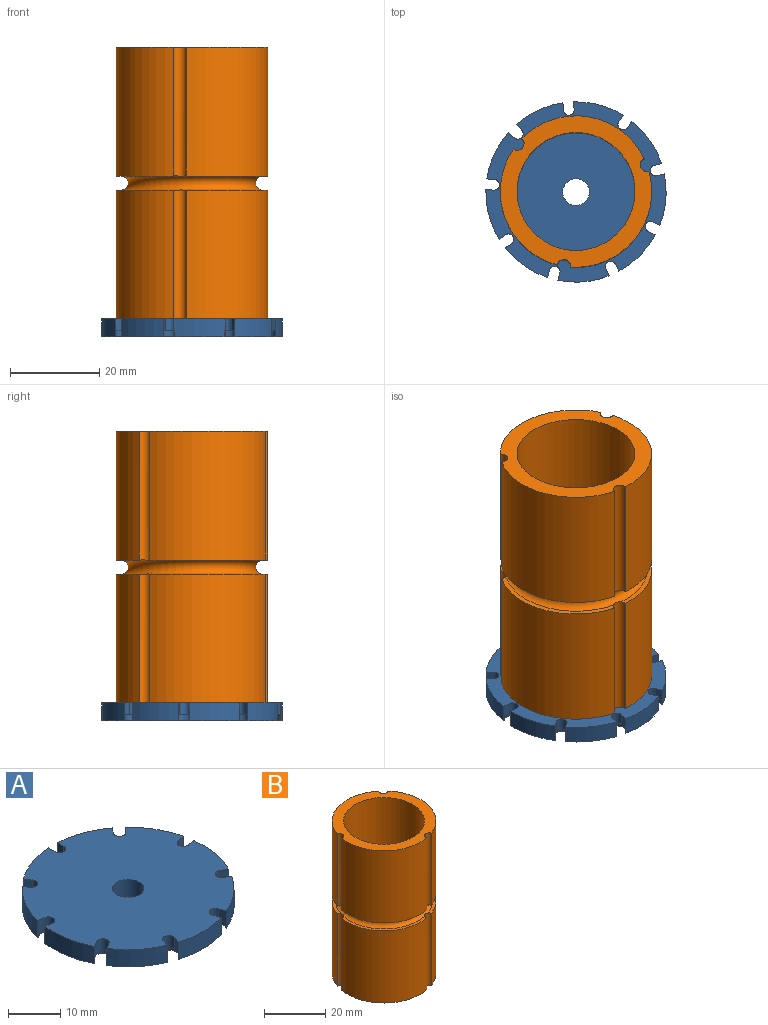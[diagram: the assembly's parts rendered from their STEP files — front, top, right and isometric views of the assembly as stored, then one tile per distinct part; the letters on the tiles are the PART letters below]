
ASSEMBLY  parts=2 mates=2
PART A: 57 faces, bbox 40.5x40.5x4 mm
  f0: plane 4x1.61mm, normal (-0.94,-0.34,0), area 4.8mm2, adj f18,f19,f37,f38,f39,f40
  f1: plane 4x1.48mm, normal (0.5,0.87,0), area 4.8mm2, adj f18,f19,f20,f38,f55,f56
  f2: plane 4x1.48mm, normal (-0.5,-0.87,0), area 4.8mm2, adj f18,f20,f21,f38,f55,f56
  f3: plane 4x1.69mm, normal (-0.17,0.98,0), area 4.8mm2, adj f18,f21,f22,f38,f53,f54
  f4: plane 4x1.69mm, normal (0.17,-0.98,0), area 4.8mm2, adj f18,f22,f23,f38,f53,f54
  f5: plane 4x1.31mm, normal (-0.77,0.64,0), area 4.8mm2, adj f18,f23,f24,f38,f51,f52
  f6: plane 4x1.31mm, normal (0.77,-0.64,0), area 4.8mm2, adj f18,f24,f25,f38,f51,f52
  f7: plane 4x1.71mm, normal (-1,0,0), area 4.8mm2, adj f18,f25,f26,f38,f49,f50
  f8: plane 4x1.71mm, normal (1,0,0), area 4.8mm2, adj f18,f26,f27,f38,f49,f50
  f9: plane 4x1.31mm, normal (-0.77,-0.64,0), area 4.8mm2, adj f18,f27,f28,f38,f47,f48
  f10: plane 4x1.31mm, normal (0.77,0.64,0), area 4.8mm2, adj f18,f28,f29,f38,f47,f48
  f11: plane 4x1.69mm, normal (-0.17,-0.98,0), area 4.8mm2, adj f18,f29,f30,f38,f45,f46
  f12: plane 4x1.69mm, normal (0.17,0.98,0), area 4.8mm2, adj f18,f30,f31,f38,f45,f46
  f13: plane 4x1.48mm, normal (0.5,-0.87,0), area 4.8mm2, adj f18,f31,f32,f38,f43,f44
  f14: plane 4x1.48mm, normal (-0.5,0.87,0), area 4.8mm2, adj f18,f32,f33,f38,f43,f44
  f15: plane 4x1.61mm, normal (0.94,-0.34,0), area 4.8mm2, adj f18,f33,f34,f38,f41,f42
  f16: plane 4x1.61mm, normal (-0.94,0.34,0), area 4.8mm2, adj f18,f34,f35,f38,f41,f42
  f17: plane 4x1.61mm, normal (0.94,0.34,0), area 4.8mm2, adj f18,f35,f37,f38,f39,f40
  f18: plane 40.5x40.46mm, normal (0,0,-1), area 1149.8mm2, adj f0,f1,f2,f3,f4,f5,f6,f7
  f19: cylinder r=20.25mm len=8.87mm, axis (0,0,-1), area 46.9mm2, adj f0,f1,f18,f38
  f20: cylinder r=1.2mm len=2.7mm, axis (0,0,-1), area 10.2mm2, adj f1,f2,f38,f56
  f21: cylinder r=20.25mm len=11.4mm, axis (0,0,-1), area 46.9mm2, adj f2,f3,f18,f38
  f22: cylinder r=1.2mm len=2.7mm, axis (0,0,-1), area 10.2mm2, adj f3,f4,f38,f54
  f23: cylinder r=20.25mm len=10.02mm, axis (0,0,-1), area 46.9mm2, adj f4,f5,f18,f38
  f24: cylinder r=1.2mm len=2.7mm, axis (0,0,-1), area 10.2mm2, adj f5,f6,f38,f52
  f25: cylinder r=20.25mm len=10.87mm, axis (0,0,-1), area 46.9mm2, adj f6,f7,f18,f38
  f26: cylinder r=1.2mm len=2.7mm, axis (0,0,-1), area 10.2mm2, adj f7,f8,f38,f50
  f27: cylinder r=20.25mm len=10.87mm, axis (0,0,-1), area 46.9mm2, adj f8,f9,f18,f38
  f28: cylinder r=1.2mm len=2.7mm, axis (0,0,-1), area 10.2mm2, adj f9,f10,f38,f48
  f29: cylinder r=20.25mm len=10.02mm, axis (0,0,-1), area 46.9mm2, adj f10,f11,f18,f38
  f30: cylinder r=1.2mm len=2.7mm, axis (0,0,-1), area 10.2mm2, adj f11,f12,f38,f46
  f31: cylinder r=20.25mm len=11.4mm, axis (0,0,-1), area 46.9mm2, adj f12,f13,f18,f38
  f32: cylinder r=1.2mm len=2.7mm, axis (0,0,-1), area 10.2mm2, adj f13,f14,f38,f44
  f33: cylinder r=20.25mm len=8.87mm, axis (0,0,-1), area 46.9mm2, adj f14,f15,f18,f38
  f34: cylinder r=1.2mm len=2.7mm, axis (0,0,-1), area 10.2mm2, adj f15,f16,f38,f42
  f35: cylinder r=20.25mm len=11.57mm, axis (0,0,-1), area 46.9mm2, adj f16,f17,f18,f38
  f36: cylinder r=3mm len=6mm, axis (0,0,-1), area 75.4mm2, adj f18,f38
  f37: cylinder r=1.2mm len=2.7mm, axis (0,0,-1), area 10.2mm2, adj f0,f17,f38,f39
  f38: plane 40.5x40.46mm, normal (0,0,1), area 1202.1mm2, adj f0,f1,f2,f3,f4,f5,f6,f7
  f39: plane 4x3.91mm, normal (0,0,-1), area 5.8mm2, adj f0,f17,f37,f40
  f40: cylinder r=2mm len=4mm, axis (0,0,-1), area 13mm2, adj f0,f17,f18,f39
  f41: cylinder r=2mm len=4mm, axis (0,0,-1), area 13mm2, adj f15,f16,f18,f42
  f42: plane 4x3.91mm, normal (0,0,-1), area 5.8mm2, adj f15,f16,f34,f41
  f43: cylinder r=2mm len=4mm, axis (0,0,-1), area 13mm2, adj f13,f14,f18,f44
  f44: plane 4x3.99mm, normal (0,0,-1), area 5.8mm2, adj f13,f14,f32,f43
  f45: cylinder r=2mm len=4mm, axis (0,0,-1), area 13mm2, adj f11,f12,f18,f46
  f46: plane 4x3.78mm, normal (0,0,-1), area 5.8mm2, adj f11,f12,f30,f45
  f47: cylinder r=2mm len=4mm, axis (0,0,-1), area 13mm2, adj f9,f10,f18,f48
  f48: plane 4x4mm, normal (0,0,-1), area 5.8mm2, adj f9,f10,f28,f47
  f49: cylinder r=2mm len=4mm, axis (0,0,-1), area 13mm2, adj f7,f8,f18,f50
  f50: plane 4x3.6mm, normal (0,0,-1), area 5.8mm2, adj f7,f8,f26,f49
  f51: cylinder r=2mm len=4mm, axis (0,0,-1), area 13mm2, adj f5,f6,f18,f52
  f52: plane 4x4mm, normal (0,0,-1), area 5.8mm2, adj f5,f6,f24,f51
  f53: cylinder r=2mm len=4mm, axis (0,0,-1), area 13mm2, adj f3,f4,f18,f54
  f54: plane 4x3.78mm, normal (0,0,-1), area 5.8mm2, adj f3,f4,f22,f53
  f55: cylinder r=2mm len=4mm, axis (0,0,-1), area 13mm2, adj f1,f2,f18,f56
  f56: plane 4x3.99mm, normal (0,0,-1), area 5.8mm2, adj f1,f2,f20,f55
PART B: 28 faces, bbox 36.9x36.9x61 mm
  f0: cylinder r=1.5mm len=28.95mm, axis (0,0,-1), area 132.4mm2, adj f1,f5,f14,f21,f25,f26
  f1: cylinder r=17mm len=28.9mm, axis (0,0,-1), area 942.2mm2, adj f0,f2,f14,f21
  f2: cylinder r=1.5mm len=28.95mm, axis (0,0,-1), area 132.4mm2, adj f1,f3,f14,f21,f22,f26
  f3: cylinder r=17mm len=28.9mm, axis (0,0,-1), area 942.2mm2, adj f2,f4,f14,f22
  f4: cylinder r=1.5mm len=28.95mm, axis (0,0,-1), area 132.4mm2, adj f3,f5,f14,f22,f25,f26
  f5: cylinder r=17mm len=28.9mm, axis (0,0,-1), area 942.2mm2, adj f0,f4,f14,f25
  f6: cylinder r=1.5mm len=28.95mm, axis (0,0,-1), area 132.4mm2, adj f7,f11,f13,f23,f26,f27
  f7: cylinder r=17mm len=28.91mm, axis (0,0,-1), area 942.7mm2, adj f6,f8,f13,f23
  f8: cylinder r=1.5mm len=28.95mm, axis (0,0,-1), area 132.4mm2, adj f7,f9,f13,f23,f24,f26
  f9: cylinder r=17mm len=28.91mm, axis (0,0,-1), area 942.7mm2, adj f8,f10,f13,f24
  f10: cylinder r=1.5mm len=28.95mm, axis (0,0,-1), area 132.4mm2, adj f9,f11,f13,f24,f26,f27
  f11: cylinder r=17mm len=28.91mm, axis (0,0,-1), area 942.7mm2, adj f6,f10,f13,f27
  f12: cylinder r=13.25mm len=61mm, axis (0,0,-1), area 5078.4mm2, adj f13,f14
  f13: plane 34x34mm, normal (0,0,1), area 346mm2, adj f6,f7,f8,f9,f10,f11,f12
  f14: plane 34x34mm, normal (0,0,-1), area 338.5mm2, adj f0,f1,f2,f3,f4,f5,f12,f15
  f15: cylinder r=0.89mm len=10mm, axis (0,0,-1), area 55.9mm2, adj f14,f16
  f16: plane 1.78x1.78mm, normal (0,0,-1), area 2.5mm2, adj f15
  f17: cylinder r=0.89mm len=10mm, axis (0,0,-1), area 55.9mm2, adj f14,f18
  f18: plane 1.78x1.78mm, normal (0,0,-1), area 2.5mm2, adj f17
  f19: cylinder r=0.89mm len=10mm, axis (0,0,-1), area 55.9mm2, adj f14,f20
  f20: plane 1.78x1.78mm, normal (0,0,-1), area 2.5mm2, adj f19
  f21: plane 20.36x19.95mm, normal (0,0,1), area 35mm2, adj f0,f1,f2,f26
  f22: plane 26.98x11.74mm, normal (0,0,1), area 35mm2, adj f2,f3,f4,f26
  f23: cone r=15.92mm half-angle=89.3deg, axis (0,0,-1), area 34.3mm2, adj f6,f7,f8,f26
  f24: cone r=15.92mm half-angle=89.3deg, axis (0,0,-1), area 34.3mm2, adj f8,f9,f10,f26
  f25: plane 26.78x12.14mm, normal (0,0,1), area 35mm2, adj f0,f4,f5,f26
  f26: torus R=15.9mm, axis (0,0,1), area 468.6mm2, adj f0,f2,f4,f6,f8,f10,f21,f22
  f27: cone r=15.92mm half-angle=89.3deg, axis (0,0,-1), area 34.3mm2, adj f6,f10,f11,f26
PLACE A rot(axis=(0,0,1),125deg) t=(-31.46,-8.92,-3.93)mm
PLACE B rot(axis=(0,0,1),95deg) t=(-31.46,-8.92,0.07)mm
MATE cylindrical B.f12 <-> A.f35  axis (0,0,-1) through (-31.46,-8.92,0.07)mm
MATE planar B.f3 <-> A.f25  axis (0,0,-1) through (-31.46,-8.92,0.07)mm
